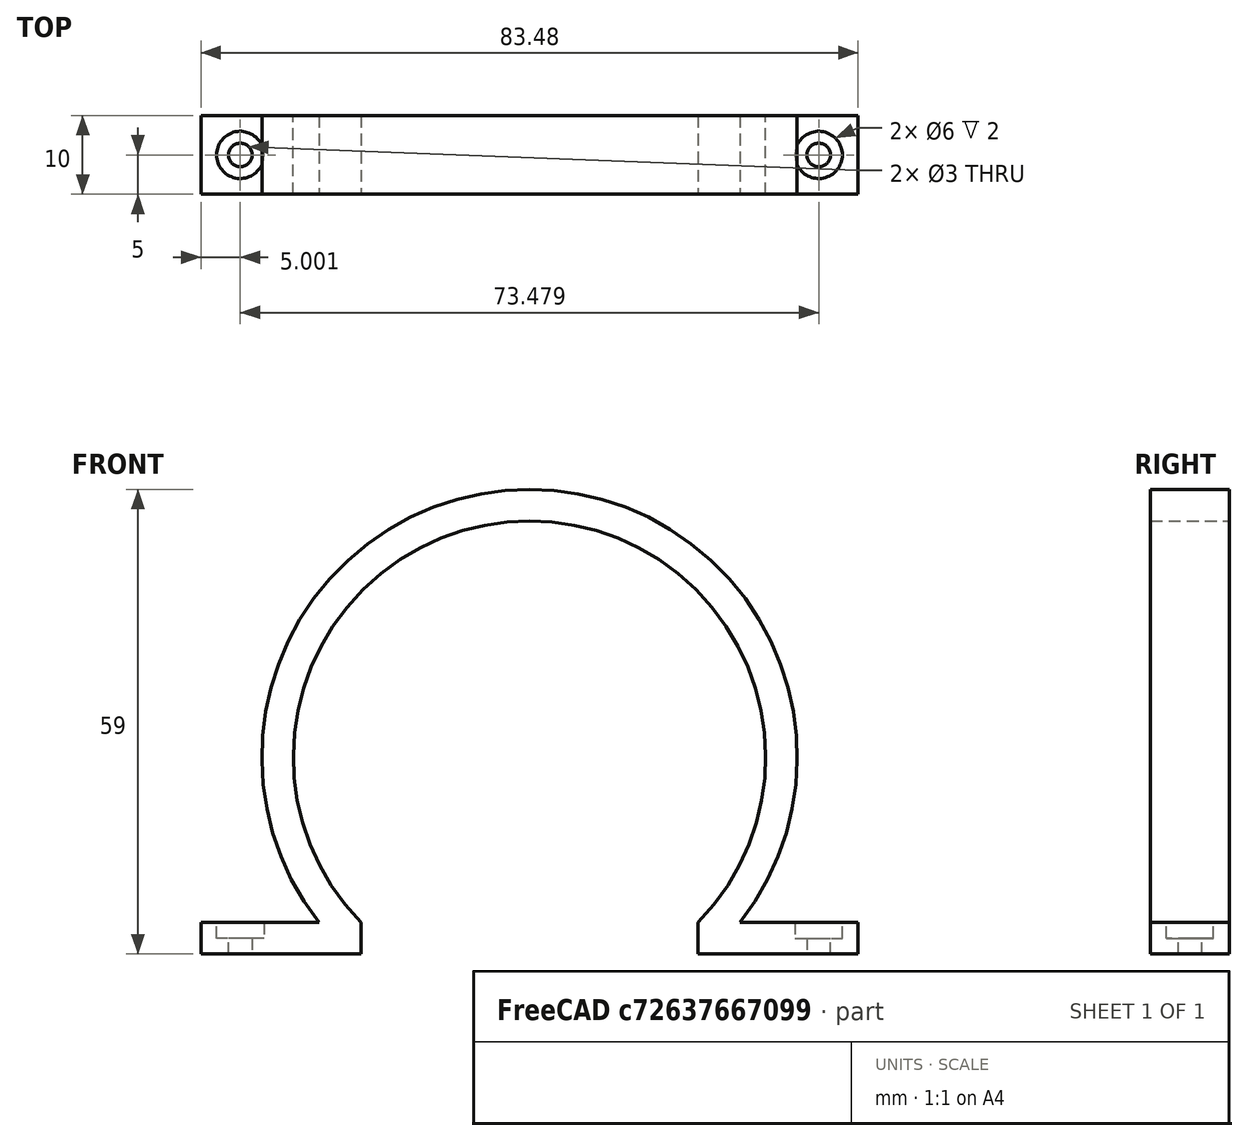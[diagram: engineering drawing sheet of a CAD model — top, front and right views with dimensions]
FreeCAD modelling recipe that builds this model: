
FCSTD DOCUMENT  (FreeCAD 1.0R39109 (Git))
Label: 50_wall_clamp
License: All rights reserved
LicenseURL: https://en.wikipedia.org/wiki/All_rights_reserved
objects: Sketcher::SketchObject×3, PartDesign::Pocket×2, PartDesign::Pad×1, PartDesign::Mirrored×1, PartDesign::Body×1, Mesh::Feature×1
note: 18 computed .brp shape members not serialized (recipe doc carries the construction recipe); baked Part::Feature solids carry a one-line shape summary decoded from their .brp

FEATURE [Sketcher::SketchObject] Sketch
  ArcFitTolerance = 1e-06
  AttachmentSupport = -> [XZ_Plane]
  FullyConstrained = true
  MakeInternals = false
  MapMode = 5
  Placement = pos=(0,0,0) rot=(1,0,0;1.5708rad)
  sketch-geometry (12):
    g0: ArcOfCircle CenterX=0 CenterY=25 CenterZ=0 NormalX=0 NormalY=0 NormalZ=1 AngleXU=0 Radius=34 StartAngle=5.61744 EndAngle=10.0905
    g1: LineSegment StartX=-26.7395 StartY=4 StartZ=0 EndX=-41.7395 EndY=4 EndZ=0
    g2: LineSegment StartX=-41.7395 StartY=4 StartZ=0 EndX=-41.7395 EndY=0 EndZ=0
    g3: LineSegment StartX=26.7395 StartY=4 StartZ=0 EndX=41.7395 EndY=4 EndZ=0
    g4: LineSegment StartX=41.7395 StartY=4 StartZ=0 EndX=41.7395 EndY=0 EndZ=0
    g5: ArcOfCircle CenterX=0 CenterY=25 CenterZ=0 NormalX=0 NormalY=0 NormalZ=1 AngleXU=0 Radius=30 StartAngle=5.50779 EndAngle=10.2002
    g6: LineSegment StartX=-41.7395 StartY=0 StartZ=0 EndX=-21.4243 EndY=0 EndZ=0
    g7: LineSegment StartX=-21.4243 StartY=0 StartZ=0 EndX=-21.4243 EndY=4 EndZ=0
    g8: LineSegment StartX=41.7395 StartY=0 StartZ=0 EndX=21.4243 EndY=0 EndZ=0
    g9: LineSegment StartX=21.4243 StartY=0 StartZ=0 EndX=21.4243 EndY=4 EndZ=0
    g10: GeomPoint X=30 Y=25 Z=0
    g11: GeomPoint X=34 Y=25 Z=0
  constraints (35):
    c: DistanceY(g-1,g0) = 25
    c: Horizontal(g0,g0)
    c: DistanceY(g-1,g0) = 4
    c: Coincident(g0,g1)
    c: Coincident(g1,g2)
    c: PointOnObject(g2,g-1)
    c: Vertical(g2)
    c: Coincident(g3,g0)
    c: Horizontal(g3)
    c: Coincident(g4,g3)
    c: PointOnObject(g4,g-1)
    c: Horizontal(g1)
    c: Vertical(g4)
    c: Equal(g1,g3)
    c: Vertical(g0,g-1)
    c: DistanceX(g1,g1) = 15
    c: Diameter(g5) = 60
    c: Coincident(g5,g0)
    c: Horizontal(g5,g0)
    c: Horizontal(g5,g0)
    c: Coincident(g6,g2)
    c: PointOnObject(g6,g-1)
    c: Coincident(g7,g6)
    c: Coincident(g7,g5)
    c: Vertical(g7)
    c: Coincident(g8,g4)
    c: PointOnObject(g8,g-1)
    c: Coincident(g9,g8)
    c: Coincident(g9,g5)
    c: Vertical(g9)
    c: PointOnObject(g10,g5)
    c: PointOnObject(g11,g0)
    c: Horizontal(g11,g10)
    c: Horizontal(g10,g0)
    c: DistanceX(g10,g11) = 4
FEATURE [PartDesign::Pad] Pad
  Direction = (0,-1,2e-16)
  Length = 10
  Length2 = 10
  Placement = pos=(0,0,0) rot=(1,0,0;1.5708rad)
  Profile = -> Sketch
  ReferenceAxis = -> Sketch [N_Axis]
  Refine = true
  Suppressed = false
  Type = 0
FEATURE [Sketcher::SketchObject] Sketch001
  ArcFitTolerance = 1e-06
  AttachmentSupport = -> [Pad]
  ExternalGeometry = -> [Pad]
  FullyConstrained = true
  MakeInternals = false
  MapMode = 5
  Placement = pos=(0,9e-16,4) rot=(0,0,1;3.14159rad)
  sketch-geometry (2):
    g0: Circle CenterX=-36.7395 CenterY=5 CenterZ=0 NormalX=0 NormalY=0 NormalZ=1 AngleXU=0 Radius=3
    g1: GeomPoint X=-41.7395 Y=5 Z=0
  constraints (4):
    c: Symmetric(g-4,g-3,g1)
    c: Horizontal(g0,g1)
    c: Diameter(g0) = 6
    c: DistanceX(g1,g0) = 5
FEATURE [PartDesign::Pocket] Pocket
  BaseFeature = -> Pad
  Direction = (0,0,-1)
  Length = 2
  Length2 = 5
  Placement = pos=(0,0,0) rot=(1,0,0;1.5708rad)
  Profile = -> Sketch001
  ReferenceAxis = -> Sketch001 [N_Axis]
  Refine = true
  Suppressed = false
  Type = 0
FEATURE [Sketcher::SketchObject] Sketch002
  ArcFitTolerance = 1e-06
  AttachmentSupport = -> [Pocket]
  ExternalGeometry = -> [Pocket]
  FullyConstrained = true
  MakeInternals = false
  MapMode = 5
  Placement = pos=(0,0,2) rot=(0,0,1;3.14159rad)
  sketch-geometry (1):
    g0: Circle CenterX=-36.7395 CenterY=5 CenterZ=0 NormalX=0 NormalY=0 NormalZ=1 AngleXU=0 Radius=1.5
  constraints (2):
    c: Coincident(g0,g-3)
    c: Diameter(g0) = 3
FEATURE [PartDesign::Pocket] Pocket001
  BaseFeature = -> Pocket
  Direction = (0,0,-1)
  Length = 5
  Length2 = 5
  Placement = pos=(0,0,0) rot=(1,0,0;1.5708rad)
  Profile = -> Sketch002
  ReferenceAxis = -> Sketch002 [N_Axis]
  Refine = true
  Suppressed = false
  Type = 0
FEATURE [PartDesign::Mirrored] Mirrored
  BaseFeature = -> Pocket001
  MirrorPlane = -> Sketch002 [V_Axis]
  Originals = -> [Pocket001,Pocket]
  Placement = pos=(0,0,0) rot=(1,0,0;1.5708rad)
  Refine = true
  Suppressed = false
  TransformMode = 0
FEATURE [PartDesign::Body] Body
  AllowCompound = false
  Group = -> [Sketch,Pad,Sketch001,Pocket,Sketch002,Pocket001,Mirrored]
  Origin = -> Origin
  Tip = -> Mirrored
FEATURE [Mesh::Feature] Mesh  label="Body (Meshed)"
